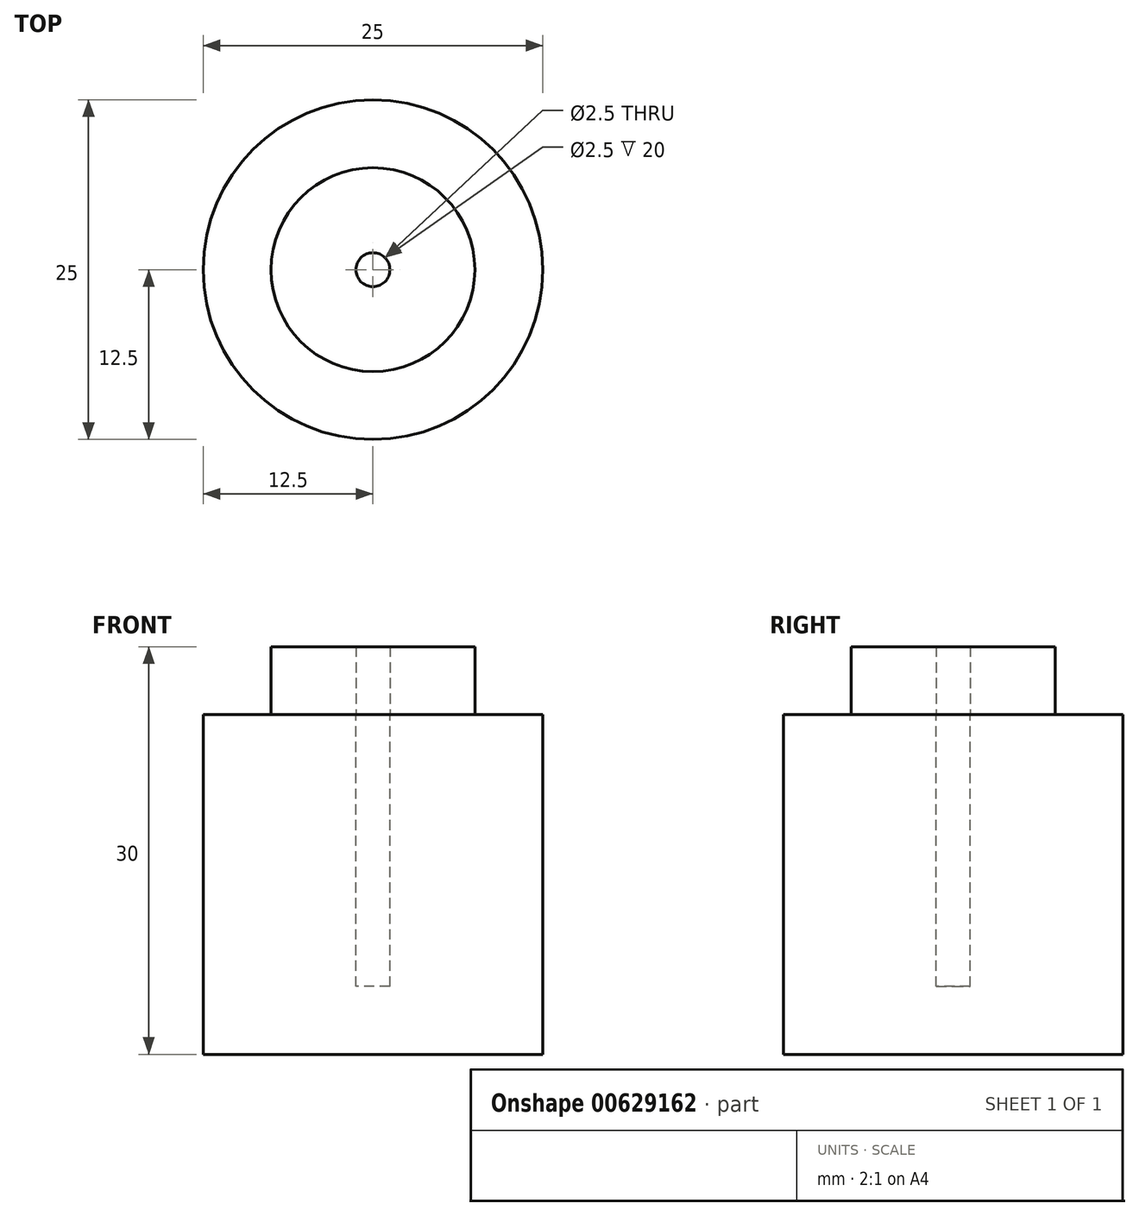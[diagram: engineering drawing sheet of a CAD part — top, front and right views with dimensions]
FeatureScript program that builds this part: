
annotation { "Feature Type Name" : "Feature", "Feature Type Description" : "" }
export const myFeature = defineFeature(function(context is Context, id is Id, definition is map)
    precondition{}
    {
        {
            var Q0;
            Q0=qCreatedBy(makeId("Top.planeOp"),FACE);
            var sketch = newSketch(context, id + "F0", { "sketchPlane" : qUnion([Q0])});
            skCircle(sketch, "E0", {"center": v(0, 0) * mm, "radius": 7.5 * mm});
            skCircle(sketch, "E1", {"center": v(0, 0) * mm, "radius": 1.25 * mm});
            skCircle(sketch, "E2", {"center": v(0, 0) * mm, "radius": 12.5 * mm});
            skSolve(sketch);
        }
        {
            var Q0;
            Q0=makeQuery(id+"F0.imprint","IMPRINT",FACE,{"disambiguationData":[TD([[makeQuery(id+"F0.imprint","IMPRINT",EDGE,{"derivedFrom":sQuery(id+"F0.wireOp",EDGE,"E0")}),-1.0]])]});
            var Q1;
            Q1=makeQuery(id+"F0.imprint","IMPRINT",FACE,{"disambiguationData":[TD([[makeQuery(id+"F0.imprint","IMPRINT",EDGE,{"derivedFrom":sQuery(id+"F0.wireOp",EDGE,"E0")}),1.0]])]});
            var Q2;
            Q2=makeQuery(id+"F0.imprint","IMPRINT",FACE,{"disambiguationData":[TD([[makeQuery(id+"F0.imprint","IMPRINT",EDGE,{"derivedFrom":sQuery(id+"F0.wireOp",EDGE,"E1")}),1.0]])]});
            extrude(context, id + "F1", {"entities" : qUnion([Q0, Q1, Q2]), "oppositeDirection" : true, "depth" : 25 * mm, "offsetDistance" : 25 * mm});
        }
        {
            var Q0;
            Q0=makeQuery(id+"F0.imprint","IMPRINT",FACE,{"disambiguationData":[TD([[makeQuery(id+"F0.imprint","IMPRINT",EDGE,{"derivedFrom":sQuery(id+"F0.wireOp",EDGE,"E1")}),1.0]])]});
            extrude(context, id + "F2", {"entities" : qUnion([Q0]), "operationType" : NewBodyOperationType.REMOVE, "oppositeDirection" : true, "depth" : 20 * mm, "offsetDistance" : 25 * mm});
        }
        {
            var Q0;
            Q0=makeQuery(id+"F0.imprint","IMPRINT",FACE,{"disambiguationData":[TD([[makeQuery(id+"F0.imprint","IMPRINT",EDGE,{"derivedFrom":sQuery(id+"F0.wireOp",EDGE,"E0")}),1.0]])]});
            extrude(context, id + "F3", {"entities" : qUnion([Q0]), "depth" : 5 * mm, "offsetDistance" : 25 * mm});
        }
    });
